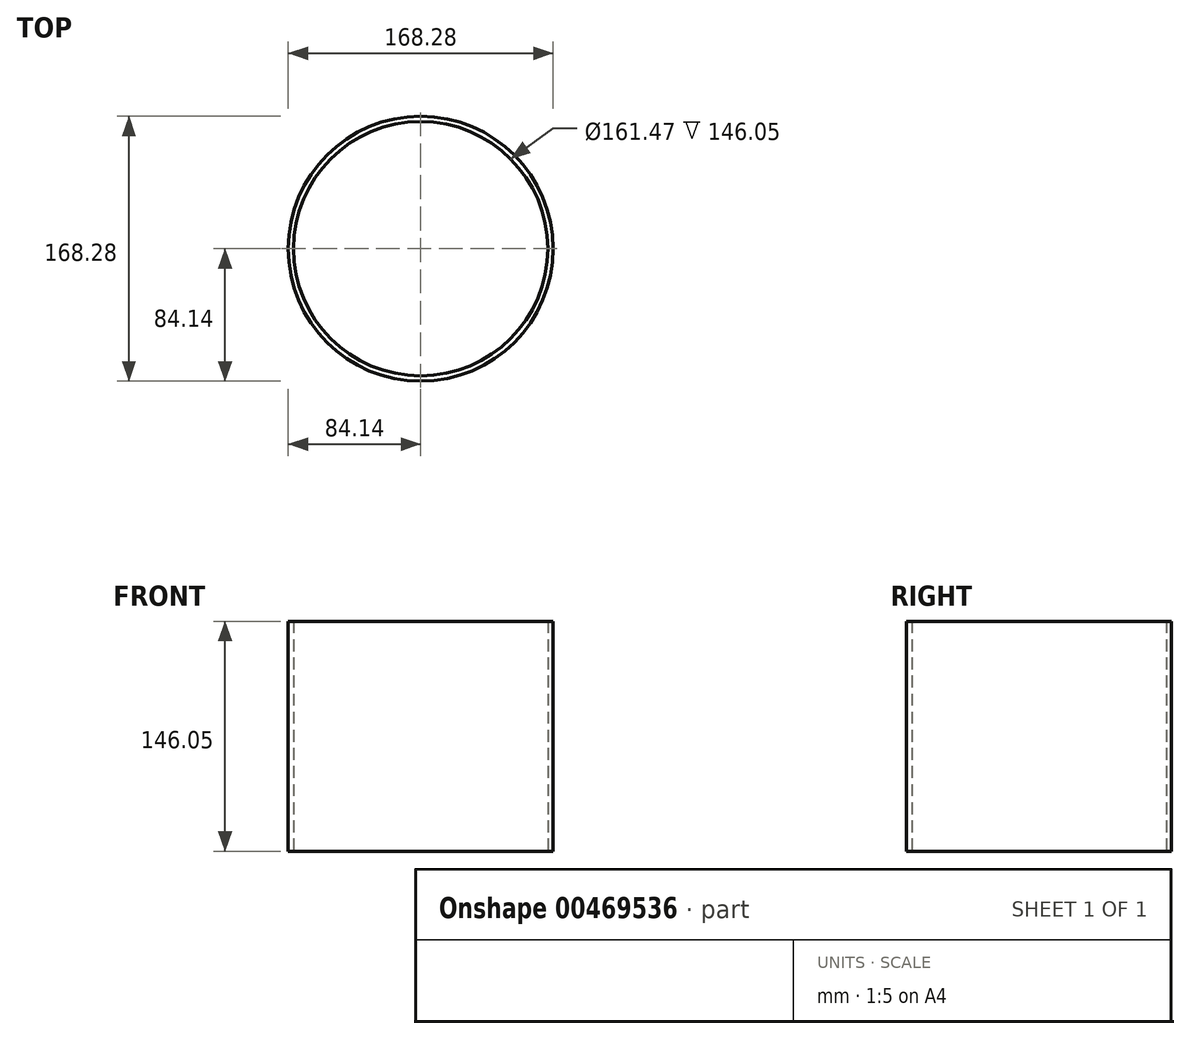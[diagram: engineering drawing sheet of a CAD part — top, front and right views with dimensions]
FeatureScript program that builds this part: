
annotation { "Feature Type Name" : "Feature", "Feature Type Description" : "" }
export const myFeature = defineFeature(function(context is Context, id is Id, definition is map)
    precondition{}
    {
        {
            var Q0;
            Q0=qCreatedBy(makeId("Top.planeOp"),FACE);
            var sketch = newSketch(context, id + "F0", { "sketchPlane" : qUnion([Q0])});
            skCircle(sketch, "E0", {"center": v(0, 0) * mm, "radius": 84.14 * mm});
            skCircle(sketch, "E1", {"center": v(0, 0) * mm, "radius": 80.73 * mm});
            skSolve(sketch);
        }
        {
            var Q0;
            Q0 = qSketchRegion(id + "F0", true);
            extrude(context, id + "F1", {"entities" : qUnion([Q0]), "depth" : 146.05 * mm, "offsetDistance" : 25.4 * mm});
        }
    });
